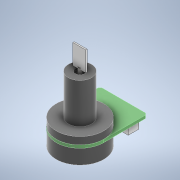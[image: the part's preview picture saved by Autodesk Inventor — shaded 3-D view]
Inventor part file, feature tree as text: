
AUTODESK INVENTOR PART (.ipt)
format: ipt  version: 2021 (Build 250183000, 183)  size: 194,048 bytes
history: native  units: mm
features: extrude x3, sketch x2, revolve x2, chamfer x1
ambient origin geometry x8: Origin, YZ Plane, XZ Plane, XY Plane, X Axis, Y Axis, Z Axis, Center Point
bodies: Solid1 (feature_tree), Solid2 (feature_tree), Solid3 (feature_tree), Solid4 (feature_tree), Solid5 (feature_tree)
feature tree (8):
  sketch  "Sketch1"  dims[d0=8.0mm d1=4.0mm]
  revolve  "Revolution1"  [1 undecoded]
  revolve  "Revolution2"  [1 undecoded]
  extrude  "Extrusion1"  Depth=22.0mm
  sketch  "Sketch2"  dims[d2=13.0mm d3=1.57mm d4=22.0mm d6=1.0mm d7=1.0mm d8=1.0mm d9=1.0mm d10=6.35mm d11=0.875mm d12=2.5mm d13=2.0mm d14=15.0mm d15=11.0mm d16=7.0mm d17=1.0mm d18=90.0deg d19=90.0deg d20=0.75mm d21=0.0mm d23=37.0mm d24=17.5mm d25=5.75mm d26=0.5mm d27=0.75mm d28=0.0mm d29=7.5mm d30=0.0mm d31=1.0mm d32=2.0mm d33=45.0deg]
  extrude  "Extrusion2"  Depth=1.0mm
  extrude  "Extrusion3"  Depth=1.0mm
  chamfer  "Chamfer1"  Distance=1.0mm
note: 2 required parameter values undecoded (feature->parameter linkage not recoverable at this tier; creation-order binding heuristic only, values carry confidence <= 0.55)
